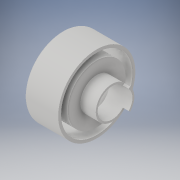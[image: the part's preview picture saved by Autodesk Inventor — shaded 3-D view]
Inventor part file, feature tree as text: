
AUTODESK INVENTOR PART (.ipt)
format: ipt  version: 2017 (Build 210142000, 142)  size: 205,312 bytes
history: native  units: in
note: dims shown in document units (in); Inventor stores cm internally (conversion verified against a paired STEP export)
features: extrude x4, sketch x3, fillet x2, plane x1, shell x1
ambient origin geometry x8: Origin, YZ Plane, XZ Plane, XY Plane, X Axis, Y Axis, Z Axis, Center Point
bodies: Solid1 (feature_tree)
feature tree (11):
  plane  "Work Plane1"
  extrude  "Wheel"  Depth=0.5906in
  extrude  "Extrusion7"  Depth=0.7087in TaperAngle=0.0deg
  fillet  "Fillet1"  Radius=1.063in
  fillet  "Fillet2"  Radius=0.6693in
  shell  "Shell1"  Thickness=0.0787in
  extrude  "Extrusion9"  Depth=0.0591in
  extrude  "Extrusion11"  Depth=0.6693in
  sketch  "Sketch7"  dims[d0=0.7874in d28=0.5906in]
  sketch  "Sketch10"  dims[d29=1.5748in d30=0.7087in d31=0.0in d33=1.063in d34=0.6693in d35=0.0in d38=0.0787in]
  sketch  "Sketch12"  dims[d39=0.0394in d40=0.0591in d41=0.6693in d42=0.315in d43=0.0in d53=0.3937in d54=0.1181in d55=0.0in]
